# Revit family: 1240_HLOS_nailfin_FXD RT_HP
name_source: partatom
category: Doors
revit_build: Autodesk Revit 2016 (Build: 20190507_1515(x64)
units: mm (PartAtom-declared; Revit-internal decimal feet)

## family parameters
Always vertical = Yes
Cut with Voids When Loaded = No
Host = Wall
OmniClass Number = 23.30.20.00
OmniClass Title = Windows
Room Calculation Point = No
Shared = No

## types (44) — shared parameters
Closed = No
Default Sill Height = 0"
Open = Yes
Setback = 1 1/8"
Wall Closure = By host

## per-type parameters (varying)
| type | Bar set | Height | Sash Width | Width_x |
| 96X96max | 39 1/4" | 96" | 36 1/4" | 96" |
| 35X80min | 23" | 80" | 20" | 35" |
| 35X86 | 23" | 86" | 20" | 35" |
| 35X92 | 23" | 92" | 20" | 35" |
| 35X96 | 23" | 96" | 20" | 35" |
| 96X92 | 39 1/4" | 92" | 36 1/4" | 96" |
| 96X80 | 39 1/4" | 80" | 36 1/4" | 96" |
| 96X86 | 39 1/4" | 86" | 36 1/4" | 96" |
| 90X80 | 39 1/4" | 80" | 36 1/4" | 90" |
| 84X80 | 39 1/4" | 80" | 36 1/4" | 84" |
| 78X80 | 39 1/4" | 80" | 36 1/4" | 78" |
| 72X80 | 39 1/4" | 80" | 36 1/4" | 72" |
| 66X80 | 39 1/4" | 80" | 36 1/4" | 66" |
| 60X80 | 39 1/4" | 80" | 36 1/4" | 60" |
| 54X80 | 39 1/4" | 80" | 36 1/4" | 54" |
| 48X80 | 36" | 80" | 33" | 48" |
| 42X80 | 30" | 80" | 27" | 42" |
| 42X86 | 30" | 86" | 27" | 42" |
| 42X92 | 30" | 92" | 27" | 42" |
| 42X96 | 30" | 96" | 27" | 42" |
| 48X86 | 36" | 86" | 33" | 48" |
| 48X92 | 36" | 92" | 33" | 48" |
| 48X96 | 36" | 96" | 33" | 48" |
| 54X86 | 39 1/4" | 86" | 36 1/4" | 54" |
| 90X86 | 39 1/4" | 86" | 36 1/4" | 90" |
| 90X92 | 39 1/4" | 92" | 36 1/4" | 90" |
| 90X96 | 39 1/4" | 96" | 36 1/4" | 90" |
| 84X86 | 39 1/4" | 86" | 36 1/4" | 84" |
| 84X92 | 39 1/4" | 92" | 36 1/4" | 84" |
| 84X96 | 39 1/4" | 96" | 36 1/4" | 84" |
| 78X86 | 39 1/4" | 86" | 36 1/4" | 78" |
| 78X92 | 39 1/4" | 92" | 36 1/4" | 78" |
| 78X96 | 39 1/4" | 96" | 36 1/4" | 78" |
| 66X86 | 39 1/4" | 86" | 36 1/4" | 66" |
| 66X92 | 39 1/4" | 92" | 36 1/4" | 66" |
| 66X96 | 39 1/4" | 96" | 36 1/4" | 66" |
| 60X86 | 39 1/4" | 86" | 36 1/4" | 60" |
| 60X92 | 39 1/4" | 92" | 36 1/4" | 60" |
| 60X96 | 39 1/4" | 96" | 36 1/4" | 60" |
| 54X92 | 39 1/4" | 92" | 36 1/4" | 54" |
| 54X96 | 39 1/4" | 96" | 36 1/4" | 54" |
| 72X86 | 39 1/4" | 86" | 36 1/4" | 72" |
| 72X92 | 39 1/4" | 92" | 36 1/4" | 72" |
| 72X96 | 39 1/4" | 96" | 36 1/4" | 72" |

## geometry (parser evidence)
native form markers: Sweep x5
no freeform markers — native parametric forms only
